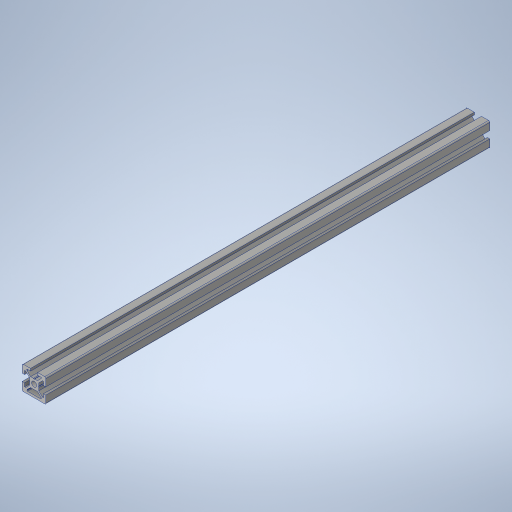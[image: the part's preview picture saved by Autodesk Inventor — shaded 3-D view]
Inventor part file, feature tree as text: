
AUTODESK INVENTOR PART (.ipt)
format: ipt  version: 2024 (Build 280153000, 153)  size: 392,704 bytes
history: native  units: mm
features: other x7, thread x2, sketch x2, extrude x1, hole x1
ambient origin geometry x8: Origin, YZ Plane, XZ Plane, XY Plane, X Axis, Y Axis, Z Axis, Center Point
bodies: Solid1 (feature_tree)
feature tree (13):
  extrude  "Extrusion1"  TaperAngle=0.0deg  [1 undecoded]
  hole  "Hole1"  [1 undecoded]
  other  "C1_XY"
  other  "C1_YZ"
  other  "C1_ZX"
  other  "C1_X"
  other  "C1_Y"
  other  "C1_Z"
  other  "C1_Center"
  thread  "Thread1"  [1 undecoded]
  thread  "Thread2"  [1 undecoded]
  sketch  "Sketch_63"  dims[d2=4.2mm d3=6.0mm d4=4.0mm d5=2.0mm d6=90.0deg d7=440.0mm d8=0.0mm d9=0.0mm d10=10.0mm d11=0.0mm d12=10.0mm d13=0.0mm]
  sketch  "Sketch2"  dims[d0=375.0mm d1=0.0mm]
note: 4 required parameter values undecoded (feature->parameter linkage not recoverable at this tier; creation-order binding heuristic only, values carry confidence <= 0.55)
